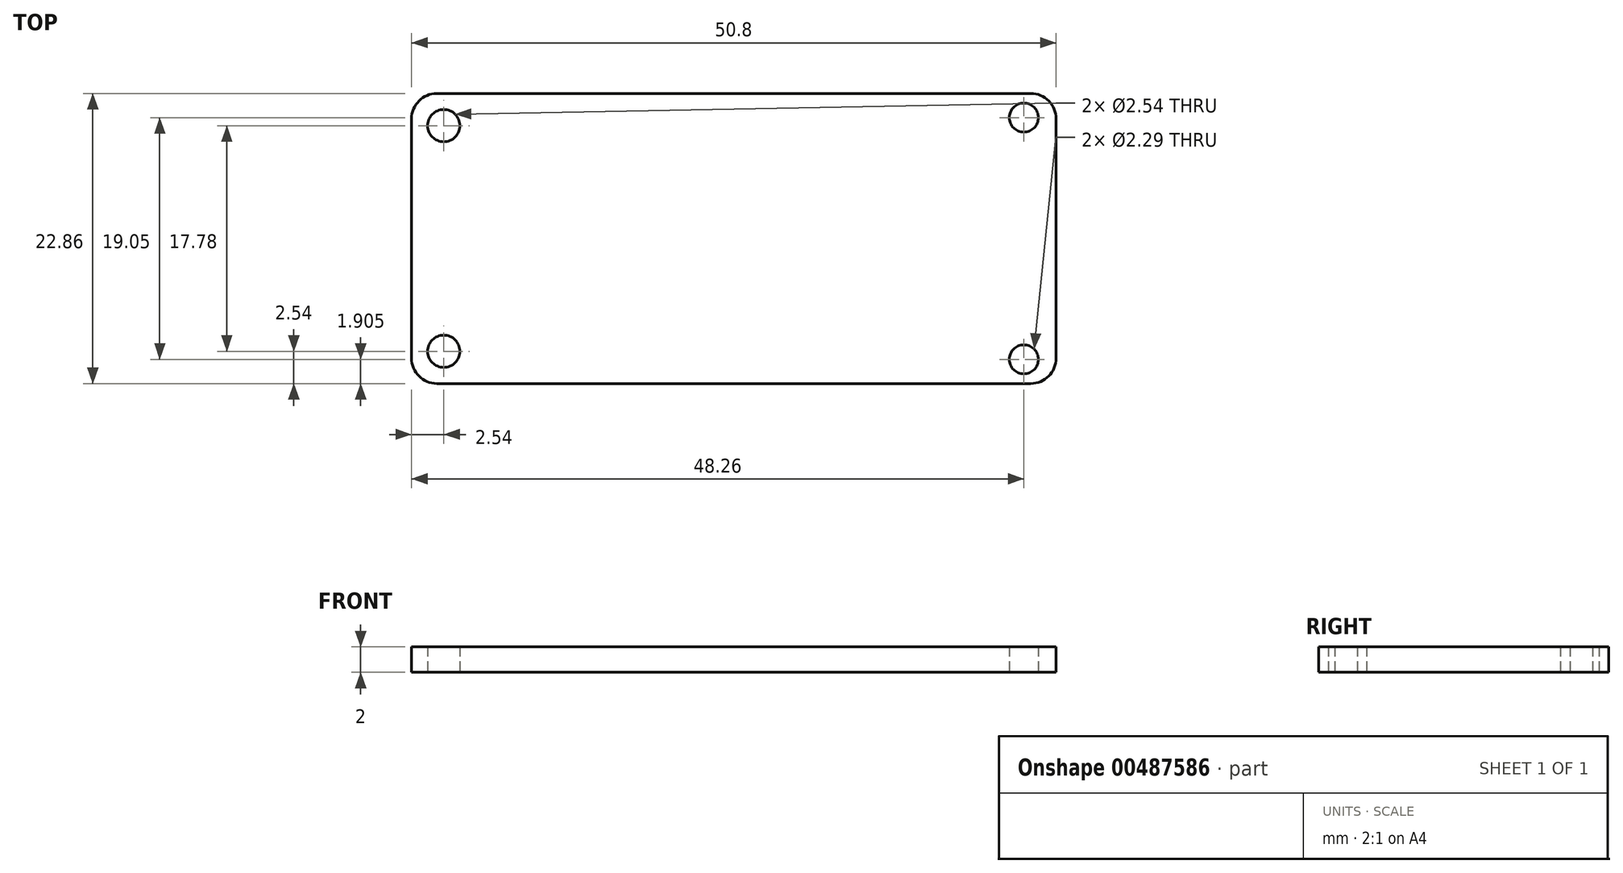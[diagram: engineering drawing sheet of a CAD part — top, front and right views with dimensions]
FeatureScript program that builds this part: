
annotation { "Feature Type Name" : "Feature", "Feature Type Description" : "" }
export const myFeature = defineFeature(function(context is Context, id is Id, definition is map)
    precondition{}
    {
        {
            var Q0;
            Q0=qCreatedBy(makeId("Top.planeOp"),FACE);
            var sketch = newSketch(context, id + "F0", { "sketchPlane" : qUnion([Q0])});
            skLineSegment(sketch, "E0.bottom", {"start": v(-23.4, 11.43) * mm, "end": v(23.4, 11.43) * mm});
            skLineSegment(sketch, "E0.top", {"start": v(-23.4, -11.43) * mm, "end": v(23.4, -11.43) * mm});
            skLineSegment(sketch, "E0.left", {"start": v(-25.4, 9.43) * mm, "end": v(-25.4, -9.43) * mm});
            skLineSegment(sketch, "E0.right", {"start": v(25.4, 9.43) * mm, "end": v(25.4, -9.43) * mm});
            skPoint(sketch, "E0.middle", {"position": v(0, 0) * mm});
            skPoint(sketch, "E1.visualSharp", {"position": v(-25.4, 11.43) * mm});
            skArc(sketch, "E1.filletArc", {"start": v(-23.4, 11.43) * mm, "mid": v(-24.81, 10.84) * mm, "end": v(-25.4, 9.43) * mm});
            skPoint(sketch, "E2.visualSharp", {"position": v(25.4, 11.43) * mm});
            skArc(sketch, "E2.filletArc", {"start": v(25.4, 9.43) * mm, "mid": v(24.81, 10.84) * mm, "end": v(23.4, 11.43) * mm});
            skPoint(sketch, "E3.visualSharp", {"position": v(25.4, -11.43) * mm});
            skArc(sketch, "E3.filletArc", {"start": v(23.4, -11.43) * mm, "mid": v(24.81, -10.84) * mm, "end": v(25.4, -9.43) * mm});
            skPoint(sketch, "E4.visualSharp", {"position": v(-25.4, -11.43) * mm});
            skArc(sketch, "E4.filletArc", {"start": v(-25.4, -9.43) * mm, "mid": v(-24.81, -10.84) * mm, "end": v(-23.4, -11.43) * mm});
            skCircle(sketch, "E5", {"center": v(-22.86, 8.9) * mm, "radius": 1.27 * mm});
            skCircle(sketch, "E6", {"center": v(22.86, 9.53) * mm, "radius": 1.14 * mm});
            skCircle(sketch, "E7.MirrorC", {"center": v(-22.86, -8.9) * mm, "radius": 1.27 * mm});
            skCircle(sketch, "E8.MirrorC", {"center": v(22.86, -9.53) * mm, "radius": 1.14 * mm});
            skSolve(sketch);
        }
        {
            var Q0;
            Q0=makeQuery(id+"F0.imprint","IMPRINT",FACE,{"disambiguationData":[TD([[makeQuery(id+"F0.imprint","IMPRINT",EDGE,{"derivedFrom":sQuery(id+"F0.wireOp",EDGE,"E0.bottom")}),-1.0]])]});
            extrude(context, id + "F1", {"entities" : qUnion([Q0]), "depth" : 2 * mm, "offsetDistance" : 25 * mm});
        }
    });
